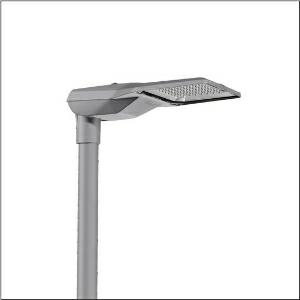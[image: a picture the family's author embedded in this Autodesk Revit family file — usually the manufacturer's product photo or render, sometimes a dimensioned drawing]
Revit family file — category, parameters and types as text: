
# Revit family: streetlight_sl_21_midi___p0_8ab_5xe3r33s08nb_ccbb
name_source: partatom
category: Lighting Fixtures
units: mm (PartAtom-declared; Revit-internal decimal feet)

## family parameters
Cut with Voids When Loaded = No
Host = Face
Light Source = No
Part Type = Normal
Room Calculation Point = No
Round Connector Dimension = Use Diameter
Shared = No

## types (1)
- --- (1 x LED, 19710 lm, 151.2 W, 3000K)
    Apparent Load = 151 VA
    CIE Flux Codes = 39 72 97 100 100
    Color Rendering = 70
    Color Temperature = 3000K
    Default Elevation = 1800 mm
    Description = Streetlight SL 21 midi, mast luminaire, primary light control with lens, of PMMA, primary optical cover: cover, of toughened safety glass, transparent, light distribution: P0.8aB, light emission: direct distribution, primary light characteristic: asymmetric, installation type: post-top, side-entry, LED, High Power LED, rated luminous flux: 19.710lm, luminous efficacy: 130lm/W, light colour: 730, colour temperature: 3000K, control gear: D4i, control: pre-setting: logarithmic dimming characteristic, flexible luminous flux parameterisation, time-dependent luminous flux control, constant luminous flux control, overheat protection, mains connection: 230..240V, AC, 50/60Hz, start of lifetime: 151W, end of service life: 157W, reduction: 70W, luminaire housing, of diecast aluminium, powder-coated, SITECO metallic grey (DB 702S), corrosivity category C5 high according to DIN EN ISO 12944, multi-level sealing system, sealing non-destructively replaceable, inclination adjustable: 0°, 5°, 10°, 15°, please order mast flange separately, length: 644mm, width: 335mm, height: 110mm, mast flange for spigot size: 42mm (side-entry): 5XC10008XM4, 60/48mm (side-entry/post-top): 5XC10108XM2, 76/60mm (side-entry/post-top): 5XC10108XM1, mounting height: 4..8m, Smart Interface above, protection rating (complete): IP66, insulation class (complete): insulation class II (safety insulation), certification: CE, ENEC, ENEC+, VDE, impact resistance: IK10, permissible operating ambient temperature for outdoor applications: -40..+50°C, standard-compliant lighting for roads and squares, packaging unit: 1 piece

Light Distribution: P0.8aB
    Height = 111 mm
    Lamp = 1 x LED
    Lamp Light Flux = 19710 lm
    Lamp Power = 151.2 W
    Lamp count = 1
    Length = 644 mm
    Luminous efficacy = 130 lm/W
    Manufacturer = Siteco
    ModVariant = No
    Model = 5XE3R33S08NB
    Number of Poles = 1
    OnlyDefault = Yes
    Power Factor = 1
    Product Name = Streetlight SL 21 midi | P0.8aB
    Product group = mast luminaire | pylon top
    ProductGroupID = 6100
    Protection Class = Protection class II
    Protection Degree = IP 66
    RLX_Detail_Level = 1
    RLX_Emergency_Light_Flux = 0 lm
    RLX_Emergency_Type = 0
    RLX_Emergency_Type_DB = No
    RlxData = <blob elided: 90233 chars, md5=ed5f98df>
    Socket = socket
    Standby Power = 0 W
    System Light Flux = 19710 lm
    System Power = 151 W
    Type Comments = factory setting: luminous flux: 100 % | dim-lin: 254 | 802 mA
    Type Image = l_1004302.jpg
    URL = http://relux.com
    VarID = @adj_078683
    Voltage = 0 V
    Weight = 0.00 kg
    Width = 336 mm

## geometry (parser evidence)
native form markers: Blend x4, Sweep x12
no freeform markers — native parametric forms only
